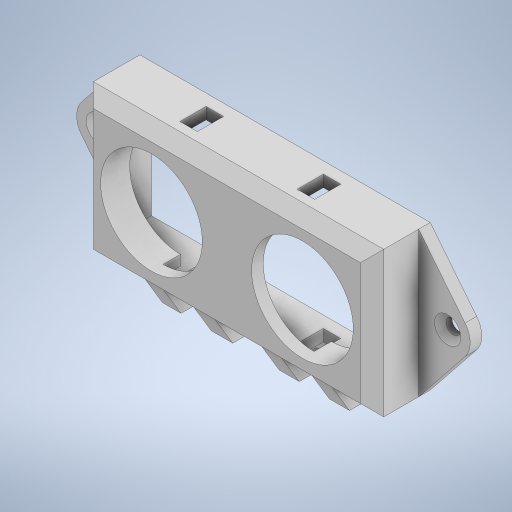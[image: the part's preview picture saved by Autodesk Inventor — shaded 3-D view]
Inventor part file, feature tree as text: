
AUTODESK INVENTOR PART (.ipt)
format: ipt  version: 2024.2 (Build 282272000, 272)  size: 409,600 bytes
history: native  units: mm
features: extrude x9, sketch x9, chamfer x2, plane x2, fillet x1
ambient origin geometry x8: Origin, YZ Plane, XZ Plane, XY Plane, X Axis, Y Axis, Z Axis, Center Point
bodies: Solid1 (feature_tree)
feature tree (23):
  extrude  "Extrusion1"  Depth=17.5mm
  extrude  "Extrusion2"  Depth=50.0mm
  extrude  "Extrusion3"  Depth=12.0mm
  chamfer  "Chamfer2"  Distance=2.0mm
  extrude  "Extrusion4"  Depth=46.0mm
  extrude  "Extrusion5"  Depth=8.0mm TaperAngle=0.0deg
  fillet  "Fillet1"  Radius=25.0mm
  chamfer  "Chamfer3"  Distance=3.0mm
  plane  "Work Plane2"
  extrude  "Extrusion6"  Depth=3.0mm
  plane  "Work Plane4"
  extrude  "Extrusion7"  Depth=17.2mm
  extrude  "Extrusion8"  Depth=1.5mm
  extrude  "Extrusion9"  Depth=3.0mm TaperAngle=0.0deg
  sketch  "Sketch1"  dims[d0=17.5mm d1=17.5mm]
  sketch  "Sketch2"  dims[d2=26.0mm d3=50.0mm]
  sketch  "Sketch3"  dims[d4=25.0mm d5=12.0mm]
  sketch  "Sketch5"  dims[d6=12.5mm d7=2.0mm d8=0.0mm]
  sketch  "Sketch6"  dims[d12=2.0mm d14=46.0mm]
  sketch  "Sketch8"  dims[d15=2.0mm d16=21.0mm d17=8.0mm d18=0.0mm d23=25.0mm d24=3.0mm d25=0.0mm]
  sketch  "Sketch10"  dims[d26=2.0mm d27=2.0mm d28=45.0deg d29=3.0mm]
  sketch  "Sketch13"  dims[d31=3.0mm d33=17.2mm]
  sketch  "Sketch14"  dims[d34=13.4mm d35=1.5mm d36=3.0mm d37=0.0mm d38=2.0mm d39=1.5mm d40=10.0mm d41=2.5mm d42=5.0mm d43=2.0mm d44=0.0mm d45=4.0mm d47=10.0mm d48=2.5mm d49=5.0mm d50=1.0mm d51=2.0mm d52=45.0deg d54=-8.9mm d56=5.0mm d57=5.0mm d58=12.1mm d59=0.0mm d60=-8.9mm d61=12.1mm d62=0.0mm d64=2.0mm d65=5.2mm d66=3.45mm d67=3.7mm d68=5.2mm d69=5.0mm d70=0.0mm d71=2.3mm d72=2.5mm d73=2.5mm d74=0.0mm d75=0.0mm d63=0.5mm]
